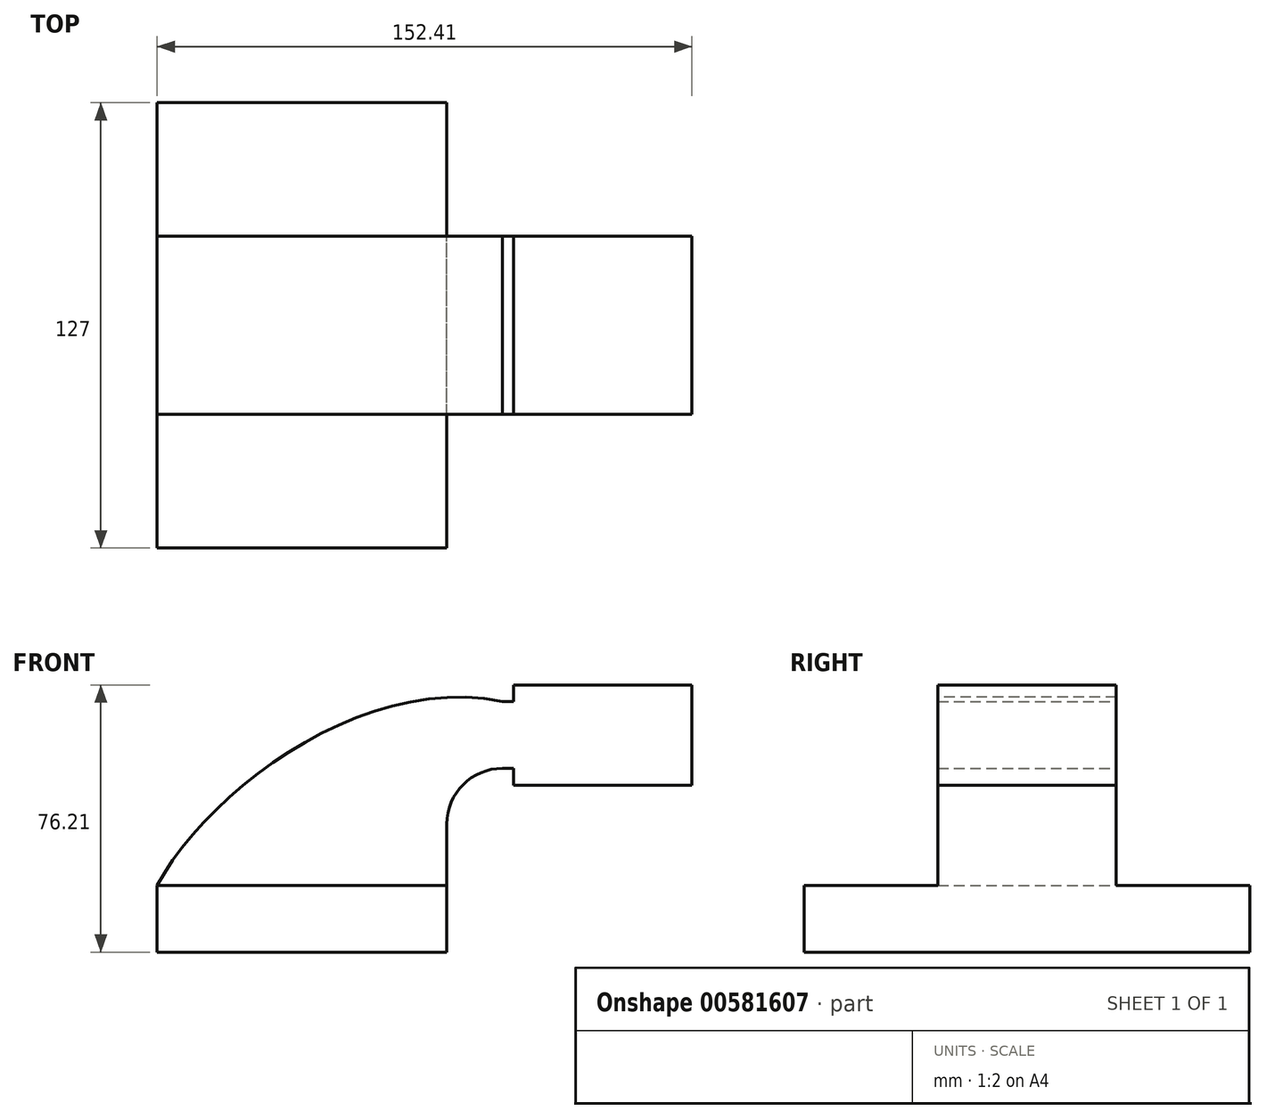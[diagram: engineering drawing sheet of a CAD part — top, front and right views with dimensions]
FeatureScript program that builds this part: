
annotation { "Feature Type Name" : "Feature", "Feature Type Description" : "" }
export const myFeature = defineFeature(function(context is Context, id is Id, definition is map)
    precondition{}
    {
        {
            var Q0;
            Q0=qCreatedBy(makeId("Front.planeOp"),FACE);
            var sketch = newSketch(context, id + "F0", { "sketchPlane" : qUnion([Q0])});
            skLineSegment(sketch, "E0.bottom", {"start": v(-41.28, -9.52) * mm, "end": v(41.28, -9.52) * mm});
            skLineSegment(sketch, "E0.top", {"start": v(-41.28, 9.53) * mm, "end": v(41.27, 9.53) * mm});
            skLineSegment(sketch, "E0.left", {"start": v(-41.27, -9.52) * mm, "end": v(-41.28, 9.53) * mm});
            skLineSegment(sketch, "E0.right", {"start": v(41.28, -9.52) * mm, "end": v(41.27, 9.53) * mm});
            skPoint(sketch, "E0.middle", {"position": v(0, 0) * mm});
            skLineSegment(sketch, "E1", {"start": v(41.27, 9.53) * mm, "end": v(41.27, 27) * mm});
            skArc(sketch, "E2", {"start": v(41.27, 27) * mm, "mid": v(45.92, 38.23) * mm, "end": v(57.15, 42.88) * mm});
            skLineSegment(sketch, "E3.bottom", {"start": v(111.13, 38.1) * mm, "end": v(60.33, 38.1) * mm});
            skLineSegment(sketch, "E3.top", {"start": v(111.13, 66.68) * mm, "end": v(60.33, 66.68) * mm});
            skLineSegment(sketch, "E3.left", {"start": v(111.13, 38.1) * mm, "end": v(111.13, 66.68) * mm});
            skLineSegment(sketch, "E3.right", {"start": v(60.33, 38.1) * mm, "end": v(60.33, 66.68) * mm});
            skPoint(sketch, "E3.middle", {"position": v(85.73, 52.39) * mm});
            skLineSegment(sketch, "E4", {"start": v(57.15, 42.88) * mm, "end": v(85.73, 42.88) * mm});
            skLineSegment(sketch, "E5.0", {"start": v(57.15, 61.93) * mm, "end": v(85.73, 61.93) * mm});
            skArc(sketch, "E5.1", {"start": v(22.23, 27) * mm, "mid": v(32.45, 51.7) * mm, "end": v(57.15, 61.93) * mm});
            skLineSegment(sketch, "E5.2", {"start": v(22.22, 9.53) * mm, "end": v(22.22, 27) * mm});
            skLineSegment(sketch, "E6", {"start": v(85.73, 38.1) * mm, "end": v(85.73, 66.68) * mm});
            skFitSpline(sketch, "E7", {"points": [v(-41.28, 9.53) * mm, v(57.15, 61.93) * mm], "startDerivative": vector(43.76, 80.87) * mm, "endDerivative": vector(119.58, -24.42) * mm});
            skSolve(sketch);
        }
        {
            var Q0;
            Q0=makeQuery(id+"F0.imprint","IMPRINT",FACE,{"disambiguationData":[TD([[makeQuery(id+"F0.imprint","IMPRINT",EDGE,{"derivedFrom":sQuery(id+"F0.wireOp",EDGE,"E0.bottom")}),1.0]])]});
            extrude(context, id + "F1", {"entities" : qUnion([Q0]), "endBound" : BoundingType.SYMMETRIC, "depth" : 127 * mm, "offsetDistance" : 25.4 * mm});
        }
        {
            var Q0;
            Q0 = qSketchRegion(id + "F0", true);
            extrude(context, id + "F2", {"entities" : qUnion([Q0]), "operationType" : NewBodyOperationType.ADD, "endBound" : BoundingType.SYMMETRIC, "depth" : 50.8 * mm, "offsetDistance" : 25.4 * mm});
        }
    });
